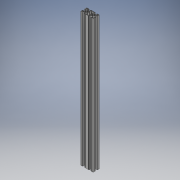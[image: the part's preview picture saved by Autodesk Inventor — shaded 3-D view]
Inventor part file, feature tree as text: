
AUTODESK INVENTOR PART (.ipt)
format: ipt  version: 2018 (Build 220112000, 112)  size: 578,048 bytes
history: native  units: mm
features: other x1, extrude x1, sketch x1
ambient origin geometry x8: Origin, YZ Plane, XZ Plane, XY Plane, X Axis, Y Axis, Z Axis, Center Point
bodies: Body1 (feature_tree)
feature tree (3):
  other  "Sólido1"
  extrude  "Extrusão1"  [1 undecoded]
  sketch  "Esboço1"  dims[d0=640.0mm d1=0.0mm]
note: 1 required parameter value undecoded (feature->parameter linkage not recoverable at this tier; creation-order binding heuristic only, values carry confidence <= 0.55)
